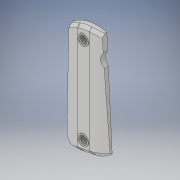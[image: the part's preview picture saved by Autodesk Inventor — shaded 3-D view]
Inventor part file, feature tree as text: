
AUTODESK INVENTOR PART (.ipt)
format: ipt  version: 2018.3 (Build 223284000, 284)  size: 292,864 bytes
history: native  units: in
note: dims shown in document units (in); Inventor stores cm internally (conversion verified against a paired STEP export)
features: extrude x7, sketch x3, chamfer x2, plane x2
ambient origin geometry x8: Origin, YZ Plane, XZ Plane, XY Plane, X Axis, Y Axis, Z Axis, Center Point
bodies: Solid1 (feature_tree)
feature tree (14):
  sketch  "Sketch1"  dims[d0=1.22in d1=0.72in]
  extrude  "Extrusion1"  Depth=0.72in
  extrude  "Extrusion2"  Depth=0.36in
  extrude  "Extrusion3"  Depth=0.1175in
  chamfer  "Chamfer1"  Distance=3.074in
  chamfer  "Chamfer2"  Distance=0.7009in
  extrude  "Extrusion4"  Depth=0.1175in
  plane  "Work Plane2"
  extrude  "Extrusion5"  Depth=0.1175in
  extrude  "Extrusion6"  Depth=0.1175in
  plane  "Work Plane3"
  extrude  "Extrusion7"  Depth=0.1175in
  sketch  "Sketch3"  dims[d2=0.91in d3=0.36in]
  sketch  "Sketch4"  dims[d4=1.542in d5=1.396in d6=3.074in d7=0.7009in d8=0.68in d9=0.63in d10=0.74in d11=1.182in d12=0.5in d13=0.25in d14=2.72in d15=0.24in d16=0.0in d17=0.38in d18=0.38in d19=0.26in d20=0.0in d25=0.06in d26=2.06in d27=0.0183in d28=2.06in d29=0.0183in d30=10.0725in d31=0.0in d32=0.225in d33=0.125in d34=45.0deg d42=0.1in d43=0.125in d44=45.0deg d45=0.238in d46=0.295in d47=0.238in d48=0.295in d49=0.885in d50=0.0in d51=0.0in d52=0.055in d53=0.0in d54=0.055in d55=0.0in d56=0.0in d57=0.1in d58=0.1175in d59=-0.1031in]
